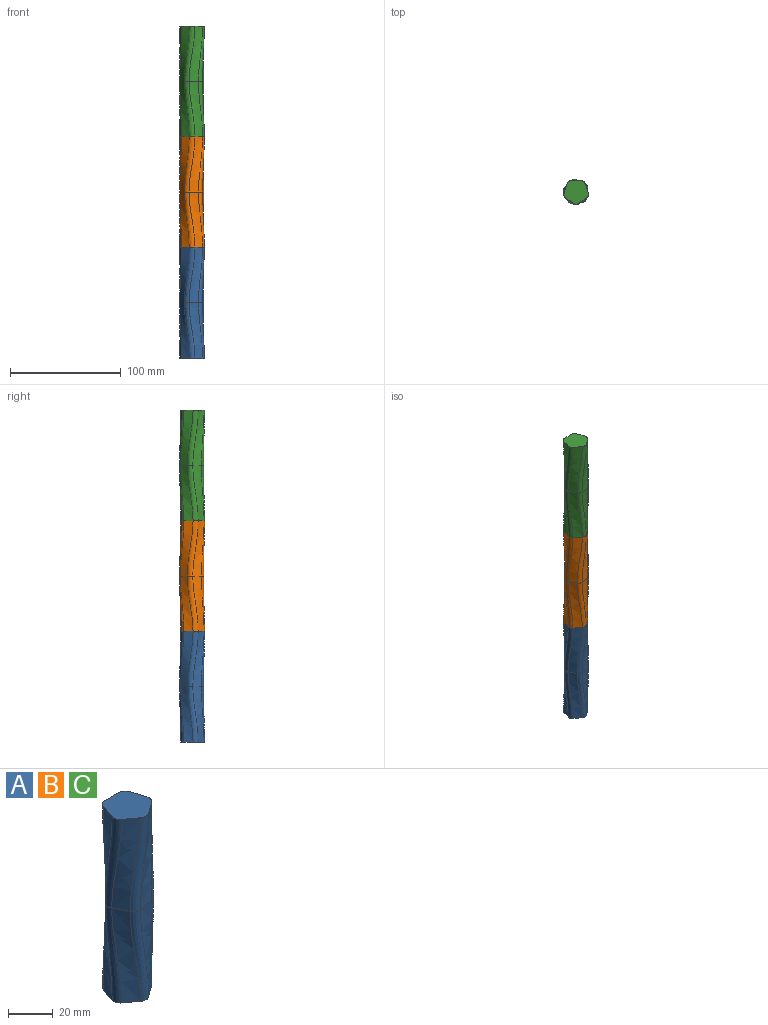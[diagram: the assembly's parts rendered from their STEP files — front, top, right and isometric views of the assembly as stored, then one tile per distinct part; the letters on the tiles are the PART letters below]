
ASSEMBLY  parts=3 mates=2
PART A: 22 faces, bbox 24x24.7x101.1 mm
  f0: plane 22.17x21.48mm, normal (0,0,-1), area 355.4mm2, adj f1,f2,f3,f4,f5,f6,f7,f8
  f1: bspline ~50x16.04mm, area 424.1mm2, adj f0,f9,f10,f12
  f2: bspline ~50x14.4mm, area 424.1mm2, adj f0,f8,f9,f13
  f3: bspline ~50x17.46mm, area 424.1mm2, adj f0,f7,f8,f14
  f4: bspline ~50x18.82mm, area 424.1mm2, adj f0,f6,f7,f15
  f5: bspline ~50x18.33mm, area 424.1mm2, adj f0,f6,f10,f16
  f6: bspline ~50.98x7.35mm, area 252.6mm2, adj f0,f4,f5,f17
  f7: bspline ~50.98x8.19mm, area 252.6mm2, adj f0,f3,f4,f18
  f8: bspline ~50.98x9.36mm, area 252.6mm2, adj f0,f2,f3,f19
  f9: bspline ~50.98x9.61mm, area 252.6mm2, adj f0,f1,f2,f20
  f10: bspline ~50.98x8.91mm, area 252.6mm2, adj f0,f1,f5,f21
  f11: plane 22.17x21.48mm, normal (0,0,1), area 355.4mm2, adj f12,f13,f14,f15,f16,f17,f18,f19
  f12: bspline ~50x16.04mm, area 424.1mm2, adj f1,f11,f20,f21
  f13: bspline ~50x14.4mm, area 424.1mm2, adj f2,f11,f19,f20
  f14: bspline ~50x17.46mm, area 424.1mm2, adj f3,f11,f18,f19
  f15: bspline ~50x18.82mm, area 424.1mm2, adj f4,f11,f17,f18
  f16: bspline ~50x18.33mm, area 424.1mm2, adj f5,f11,f17,f21
  f17: bspline ~50.98x7.35mm, area 252.6mm2, adj f6,f11,f15,f16
  f18: bspline ~50.98x8.19mm, area 252.6mm2, adj f7,f11,f14,f15
  f19: bspline ~50.98x9.36mm, area 252.6mm2, adj f8,f11,f13,f14
  f20: bspline ~50.98x9.61mm, area 252.6mm2, adj f9,f11,f12,f13
  f21: bspline ~50.98x8.91mm, area 252.6mm2, adj f10,f11,f12,f16
PART B: same geometry as A
PART C: same geometry as A
PLACE A at identity
PLACE B t=(0,0,100)mm
PLACE C t=(0,0,200)mm
MATE fastened C.f0 <-> B.f11  axis (0,0,-1) through (0,0,200)mm
MATE fastened B.f0 <-> A.f11  axis (0,0,-1) through (0,0,100)mm
